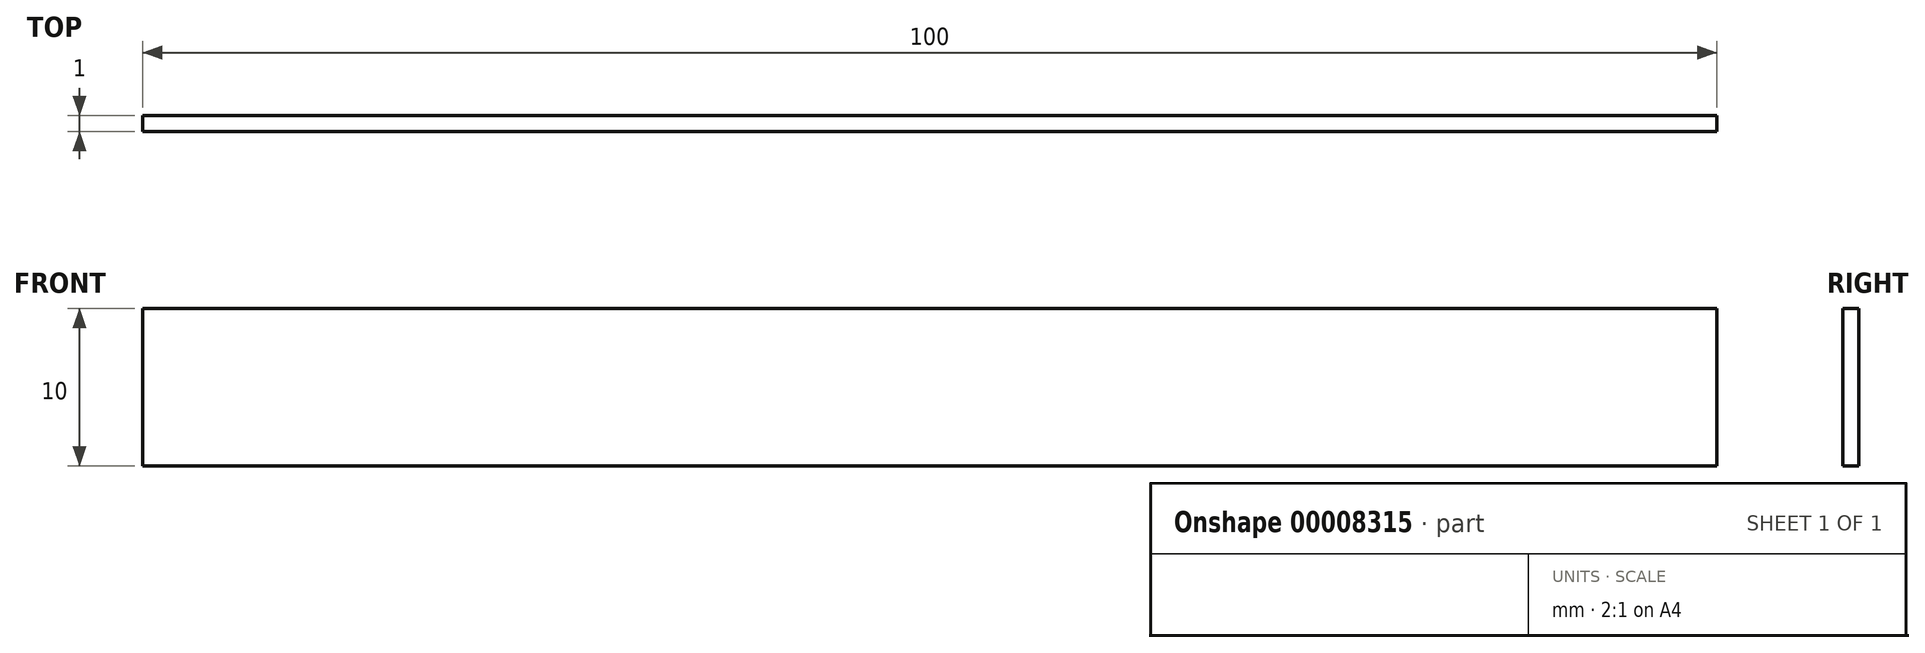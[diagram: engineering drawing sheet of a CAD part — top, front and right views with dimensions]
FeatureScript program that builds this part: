
annotation { "Feature Type Name" : "Feature", "Feature Type Description" : "" }
export const myFeature = defineFeature(function(context is Context, id is Id, definition is map)
    precondition{}
    {
        {
            var Q0;
            Q0=qCreatedBy(makeId("Front.planeOp"),FACE);
            var sketch = newSketch(context, id + "F0", { "sketchPlane" : qUnion([Q0])});
            skLineSegment(sketch, "E0.bottom", {"start": v(0, 0) * mm, "end": v(100, 0) * mm});
            skLineSegment(sketch, "E0.top", {"start": v(0, 10) * mm, "end": v(100, 10) * mm});
            skLineSegment(sketch, "E0.left", {"start": v(0, 0) * mm, "end": v(0, 10) * mm});
            skLineSegment(sketch, "E0.right", {"start": v(100, 0) * mm, "end": v(100, 10) * mm});
            skSolve(sketch);
        }
        {
            var Q0;
            Q0 = qSketchRegion(id + "F0", true);
            var Q1;
            Q1=sQuery(id+"F0.wireOp",EDGE,"E0.top");
            var Q2;
            Q2=sQuery(id+"F0.wireOp",EDGE,"E0.bottom");
            var Q3;
            Q3=sQuery(id+"F0.wireOp",EDGE,"E0.left");
            var Q4;
            Q4=sQuery(id+"F0.wireOp",EDGE,"E0.right");
            extrude(context, id + "F1", {"entities" : qUnion([Q0]), "surfaceEntities" : qUnion([Q1, Q2, Q3, Q4]), "depth" : 1 * mm});
        }
    });
